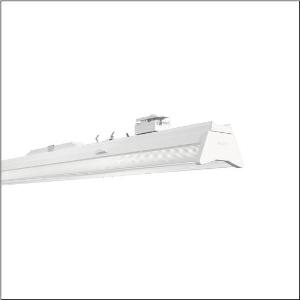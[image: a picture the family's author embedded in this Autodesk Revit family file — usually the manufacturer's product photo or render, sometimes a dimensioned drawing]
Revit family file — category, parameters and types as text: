
# Revit family: licross_r__11_performance_mo_51td16mn4axg_aad5
name_source: partatom
category: Lighting Fixtures
units: mm (PartAtom-declared; Revit-internal decimal feet)

## family parameters
Cut with Voids When Loaded = No
Host = Face
Light Source = No
Part Type = Normal
Room Calculation Point = No
Round Connector Dimension = Use Diameter
Shared = No

## types (1)
- --- (1 x LED, 10160 lm, 55.3 W, 4000K)
    Apparent Load = 55 VA
    CIE Flux Codes = 66 88 96 79 100
    Color Rendering = 80
    Color Temperature = 4000K
    Default Elevation = 1800 mm
    Description = Licross® 11 Performance MO, luminaire insert, of sheet steel, galvanised, coil coated, white, length: 1.500mm, width: 120mm, height: 123mm, LED rated luminous flux: 10.160lm, light colour: 840, control gear: ON/OFF Multilumen, with plug, 3-pole, with phase selection, mains connection: 220..240V, AC, 50/60Hz, rated input power: 55W, halogen-free wiring, primary light control with lens, of plastic, primary optical cover: cover, of PMMA, light emission: direct/indirect distribution, primary light characteristic: symmetric, protection rating (complete): IP54, insulation class (complete): insulation class I (protective earthing), certification: CE, ENEC, VDE, UKCA, protection symbol: D if used in an environment with non-conductive dust loads with corresponding accessories, impact resistance: IK06, permissible ambient temperature for indoor applications: -35..+40°C, corresponds to IFS (International Featured Standards) requirements for safety and quality in the food industry, reducing of maximum allowable ambient temperature of 5°C with ceiling mounting, LABS conformity tested according to VDMA 24364:2018-05, packaging unit: 1 piece
    Height = 114 mm
    Lamp = 1 x LED
    Lamp Light Flux = 10160 lm
    Lamp Power = 55.3 W
    Lamp count = 1
    Length = 1500 mm
    Luminous efficacy = 184 lm/W
    Manufacturer = Siteco
    ModVariant = No
    Model = 51TD16MN4AXG
    Mounting Place = Ceiling
    Mounting Type = Pendant
    Number of Poles = 1
    OnlyDefault = Yes
    Power Factor = 1
    Product Name = Licross® 11 Performance MO
    Product group = luminaire insert
    ProductGroupID = 901
    Protection Class = Protection class I
    Protection Degree = IP 54
    RLX_Detail_Level = 1
    RLX_Emergency_Light_Flux = 0 lm
    RLX_Emergency_Type = 0
    RLX_Emergency_Type_DB = No
    RlxData = <blob elided: 31837 chars, md5=59a2ba98>
    Socket = socket
    Standby Power = 0 W
    System Light Flux = 10160 lm
    System Power = 55 W
    Type Comments = factory setting: luminous flux: 100 % | (A | C | E) | 126 mA
    Type Image = l_1256138.jpg
    URL = http://relux.com
    VarID = @adj_055467
    Voltage = 0 V
    Weight = 0.00 kg
    Width = 120 mm

## geometry (parser evidence)
native form markers: Blend x4, Sweep x12
no freeform markers — native parametric forms only
